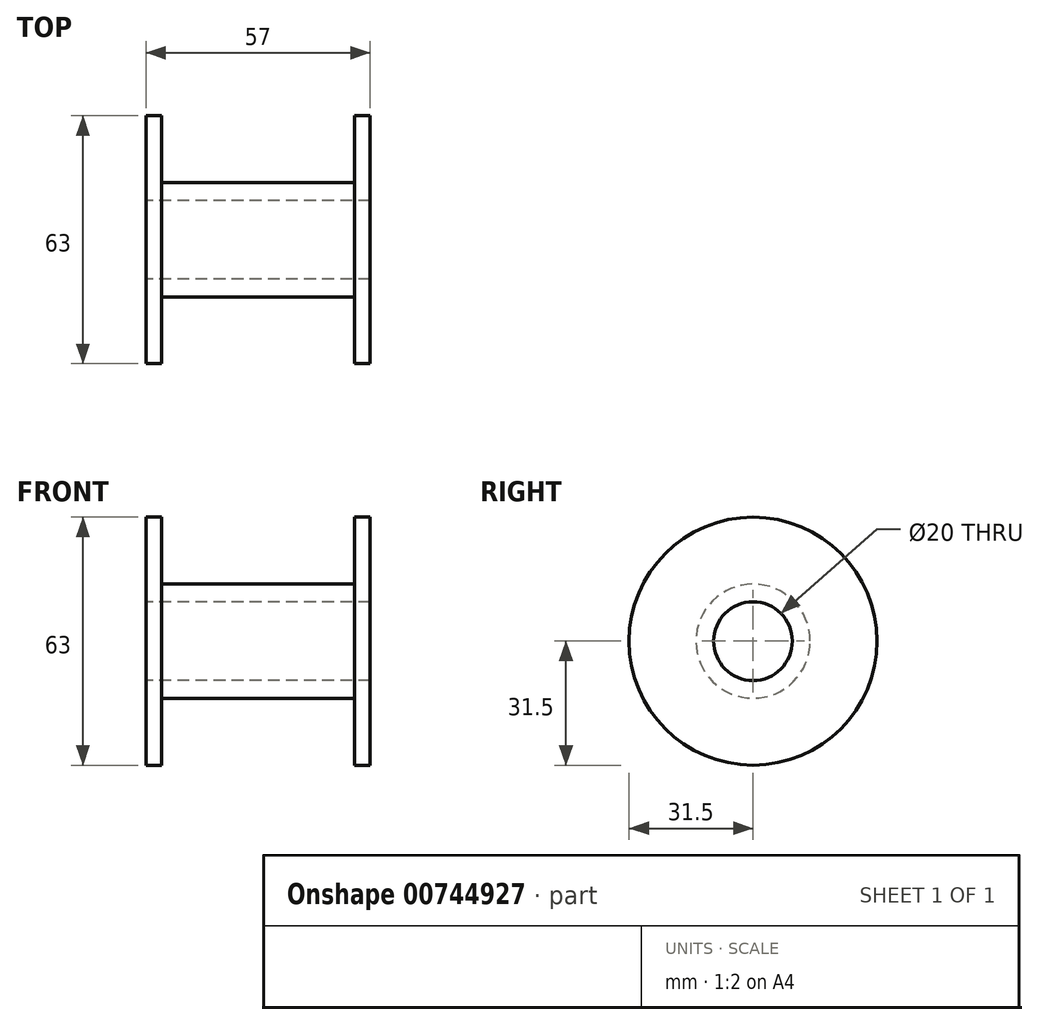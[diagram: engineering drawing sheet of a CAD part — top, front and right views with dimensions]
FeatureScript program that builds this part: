
annotation { "Feature Type Name" : "Feature", "Feature Type Description" : "" }
export const myFeature = defineFeature(function(context is Context, id is Id, definition is map)
    precondition{}
    {
        {
            var Q0;
            Q0=qCreatedBy(makeId("Front.planeOp"),FACE);
            var sketch = newSketch(context, id + "F0", { "sketchPlane" : qUnion([Q0])});
            skLineSegment(sketch, "E0", {"start": v(0, 10) * mm, "end": v(-28.5, 10) * mm});
            skLineSegment(sketch, "E1", {"start": v(-28.5, 10) * mm, "end": v(-28.5, 31.5) * mm});
            skLineSegment(sketch, "E2", {"start": v(-28.5, 31.5) * mm, "end": v(-24.5, 31.5) * mm});
            skLineSegment(sketch, "E3", {"start": v(-24.5, 31.5) * mm, "end": v(-24.5, 14.5) * mm});
            skLineSegment(sketch, "E4", {"start": v(-24.5, 14.5) * mm, "end": v(0, 14.5) * mm});
            skLineSegment(sketch, "E5", {"start": v(0, 14.5) * mm, "end": v(0, 10) * mm});
            skLineSegment(sketch, "E6.MirrorCS", {"start": v(28.5, 31.5) * mm, "end": v(24.5, 31.5) * mm});
            skLineSegment(sketch, "E7.MirrorCS", {"start": v(28.5, 10) * mm, "end": v(28.5, 31.5) * mm});
            skLineSegment(sketch, "E8.MirrorCS", {"start": v(24.5, 31.5) * mm, "end": v(24.5, 14.5) * mm});
            skLineSegment(sketch, "E9.MirrorCS", {"start": v(0, 10) * mm, "end": v(28.5, 10) * mm});
            skLineSegment(sketch, "E10.MirrorCS", {"start": v(24.5, 14.5) * mm, "end": v(0, 14.5) * mm});
            skLineSegment(sketch, "E11", {"start": v(-32.2, 0) * mm, "end": v(35.88, 0) * mm});
            skSolve(sketch);
        }
        {
            var Q0;
            Q0 = qSketchRegion(id + "F0", true);
            var Q1;
            Q1=sQuery(id+"F0.wireOp",EDGE,"E11");
            revolve(context, id + "F1", {"surfaceOperationType" : NewSurfaceOperationType.NEW, "entities" : qUnion([Q0]), "axis" : qUnion([Q1]), "revolveType" : RevolveType.FULL});
        }
    });
